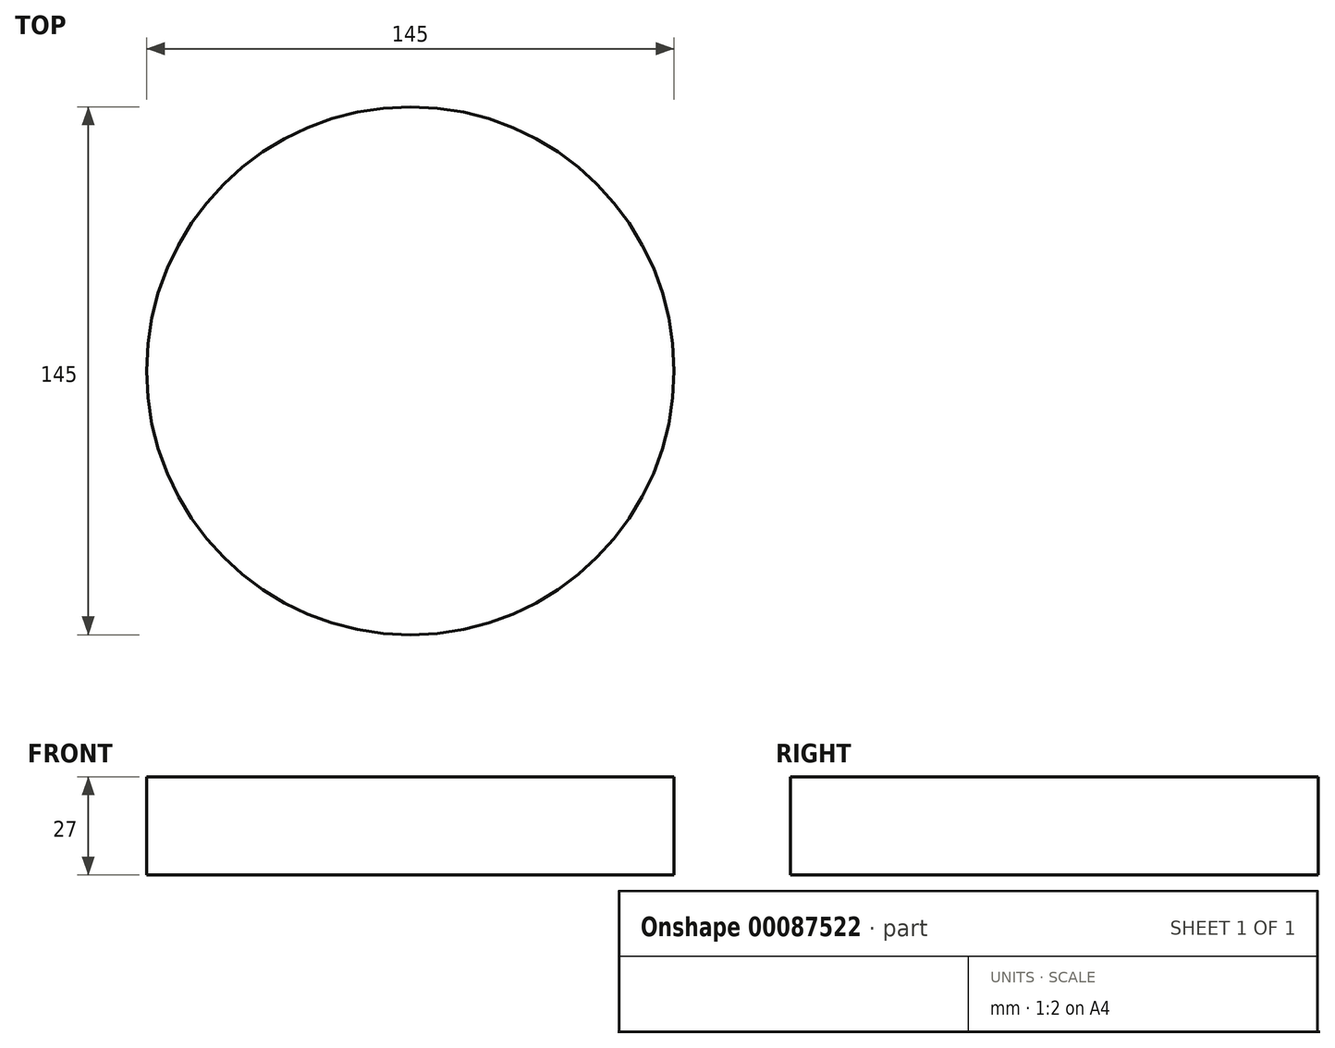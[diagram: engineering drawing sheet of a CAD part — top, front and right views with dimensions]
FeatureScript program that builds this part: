
annotation { "Feature Type Name" : "Feature", "Feature Type Description" : "" }
export const myFeature = defineFeature(function(context is Context, id is Id, definition is map)
    precondition{}
    {
        {
            var Q0;
            Q0=qCreatedBy(makeId("Top.planeOp"),FACE);
            var sketch = newSketch(context, id + "F0", { "sketchPlane" : qUnion([Q0])});
            skCircle(sketch, "E0", {"center": v(0, 0) * mm, "radius": 72.5 * mm});
            skSolve(sketch);
        }
        {
            var Q0;
            Q0=makeQuery(id+"F0.imprint","IMPRINT",FACE,{"disambiguationData":[TD([[makeQuery(id+"F0.imprint","IMPRINT",EDGE,{"derivedFrom":sQuery(id+"F0.wireOp",EDGE,"E0")}),1.0]])]});
            var Q1;
            Q1=sQuery(id+"F0.wireOp",EDGE,"E0");
            extrude(context, id + "F1", {"entities" : qUnion([Q0]), "surfaceEntities" : qUnion([Q1]), "depth" : 27 * mm});
        }
    });
